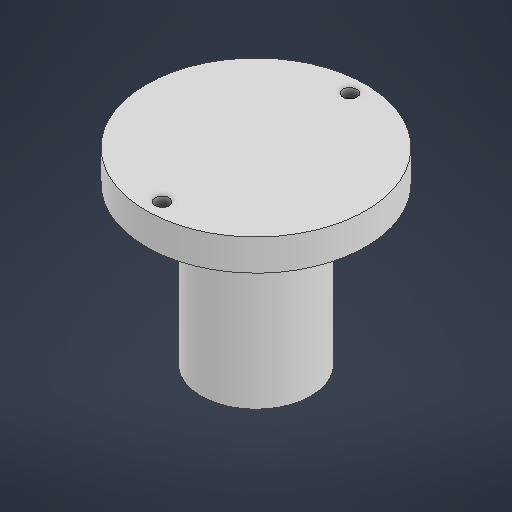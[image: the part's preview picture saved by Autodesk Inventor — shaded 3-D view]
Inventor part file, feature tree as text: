
AUTODESK INVENTOR PART (.ipt)
format: ipt  version: 2025 (Build 290162000, 162)  size: 190,464 bytes
history: native  units: in
note: dims shown in document units (in); Inventor stores cm internally (conversion verified against a paired STEP export)
features: extrude x2, sketch x2
ambient origin geometry x8: Origin, YZ Plane, XZ Plane, XY Plane, X Axis, Y Axis, Z Axis, Center Point
bodies: Solid1 (feature_tree)
feature tree (4):
  extrude  "Extrusion1"  Depth=2.3622in
  extrude  "Extrusion2"  Depth=1.9685in
  sketch  "Sketch1"  dims[d0=2.7559in d1=2.3622in]
  sketch  "Sketch2"  dims[d2=0.1772in d3=0.1772in d4=0.3937in d5=0.0in d6=1.378in d7=1.9685in d8=0.0in]
